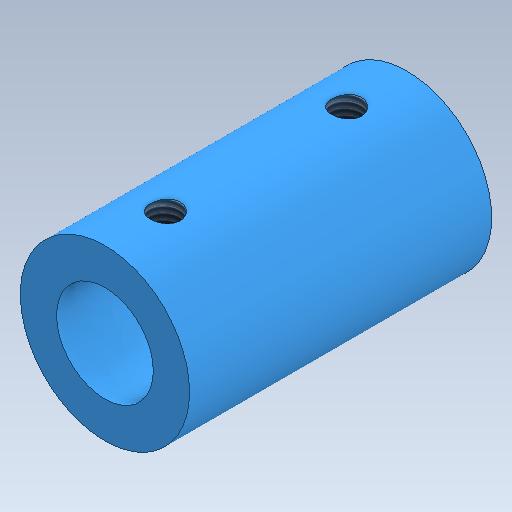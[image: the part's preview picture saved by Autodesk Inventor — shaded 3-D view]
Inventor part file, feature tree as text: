
AUTODESK INVENTOR PART (.ipt)
format: ipt  version: 2020 (Build 240168000, 168)  size: 145,408 bytes
history: native  units: mm
features: sketch x3, hole x2, extrude x1
ambient origin geometry x8: Origin, YZ Plane, XZ Plane, XY Plane, X Axis, Y Axis, Z Axis, Center Point
bodies: Solid1 (feature_tree)
feature tree (6):
  extrude  "Extrusion1"  Depth=25.0mm TaperAngle=0.0deg
  hole  "Hole1"  [1 undecoded]
  hole  "Hole2"  [1 undecoded]
  sketch  "Sketch1"  dims[d0=14.0mm d1=25.0mm d2=0.0mm]
  sketch  "Sketch3"  dims[d3=5.0mm d4=6.0mm d5=8.0mm d6=12.5mm d7=90.0deg d8=8.0mm d9=20.594885mm d10=5.0mm]
  sketch  "Sketch4"  dims[d11=5.0mm d12=2.459mm d13=8.0mm d14=8.0mm d15=12.5mm d16=90.0deg d17=8.8mm d18=20.594885mm]
note: 2 required parameter values undecoded (feature->parameter linkage not recoverable at this tier; creation-order binding heuristic only, values carry confidence <= 0.55)
